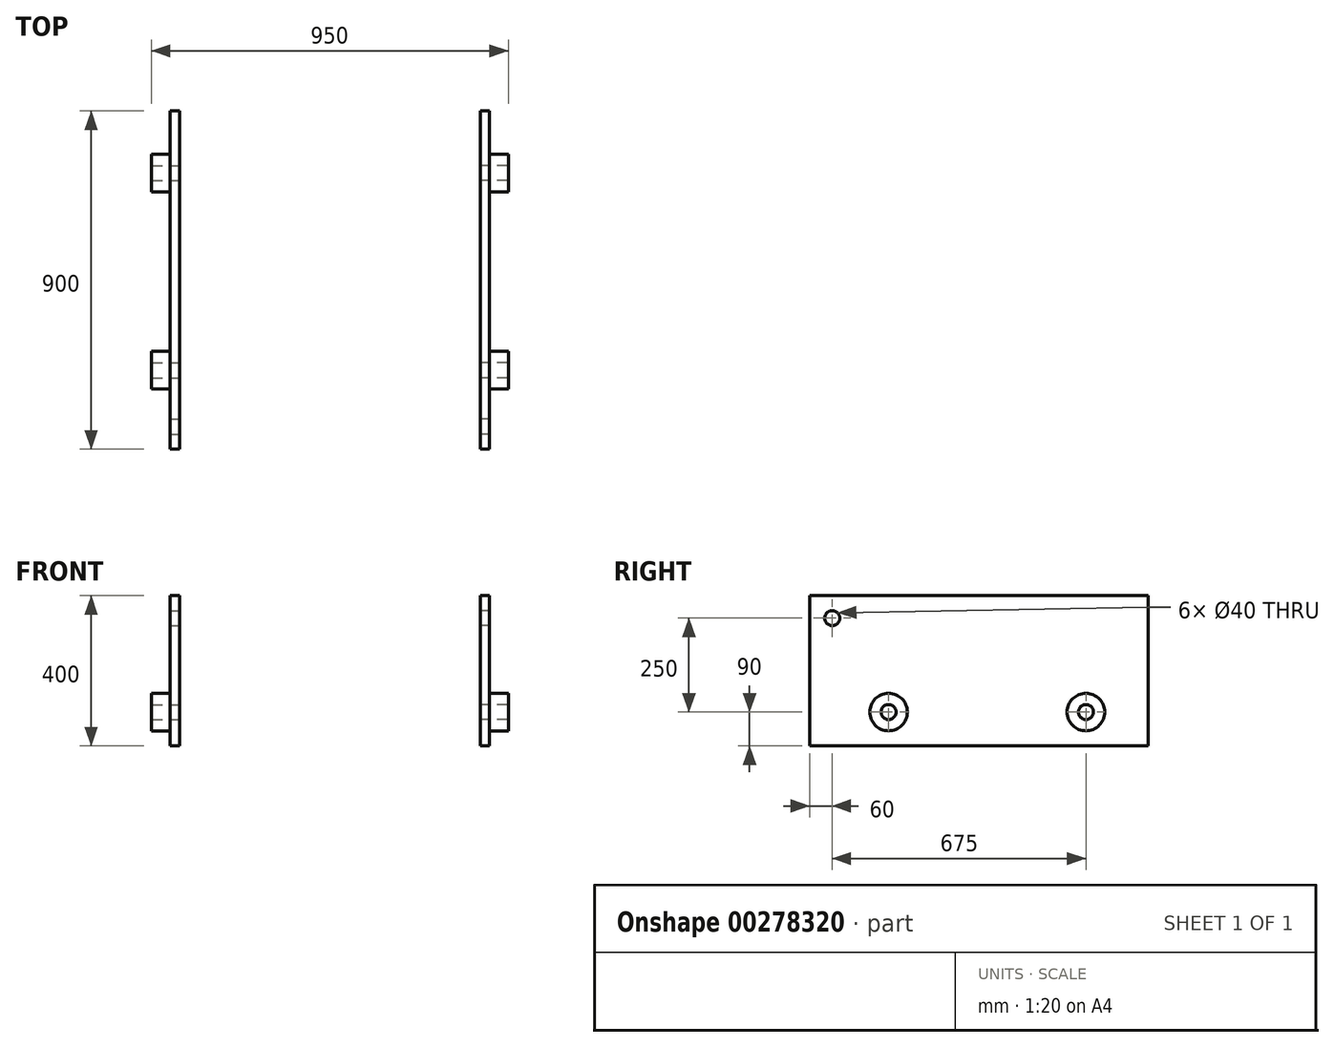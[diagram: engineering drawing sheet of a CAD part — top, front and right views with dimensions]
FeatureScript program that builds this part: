
annotation { "Feature Type Name" : "Feature", "Feature Type Description" : "" }
export const myFeature = defineFeature(function(context is Context, id is Id, definition is map)
    precondition{}
    {
        {
            var Q0;
            Q0=qCreatedBy(makeId("Right.planeOp"),FACE);
            var sketch = newSketch(context, id + "F0", { "sketchPlane" : qUnion([Q0])});
            skLineSegment(sketch, "E0.bottom", {"start": v(0, 0) * mm, "end": v(900, 0) * mm});
            skLineSegment(sketch, "E0.top", {"start": v(0, 400) * mm, "end": v(900, 400) * mm});
            skLineSegment(sketch, "E0.left", {"start": v(0, 0) * mm, "end": v(0, 400) * mm});
            skLineSegment(sketch, "E0.right", {"start": v(900, 0) * mm, "end": v(900, 400) * mm});
            skCircle(sketch, "E1", {"center": v(60, 340) * mm, "radius": 20 * mm});
            skCircle(sketch, "E2", {"center": v(210, 90) * mm, "radius": 20 * mm});
            skCircle(sketch, "E3", {"center": v(735, 90) * mm, "radius": 20 * mm});
            skSolve(sketch);
        }
        {
            var Q0;
            Q0=makeQuery(id+"F0.imprint","IMPRINT",FACE,{"disambiguationData":[TD([[makeQuery(id+"F0.imprint","IMPRINT",EDGE,{"derivedFrom":sQuery(id+"F0.wireOp",EDGE,"E0.bottom")}),1.0]])]});
            extrude(context, id + "F1", {"entities" : qUnion([Q0]), "depth" : 25 * mm});
        }
        {
            var Q0;
            Q0=makeQuery(id+"F1.opExtrude","CAP_FACE",FACE,{"disambiguationData":[OSD([sQuery(id+"F0.wireOp",EDGE,"E0.bottom"),sQuery(id+"F0.wireOp",EDGE,"E0.top"),sQuery(id+"F0.wireOp",EDGE,"E0.left"),sQuery(id+"F0.wireOp",EDGE,"E0.right"),sQuery(id+"F0.wireOp",EDGE,"E1"),sQuery(id+"F0.wireOp",EDGE,"E2"),sQuery(id+"F0.wireOp",EDGE,"E3")])],"isStart":false});
            var sketch = newSketch(context, id + "F2", { "sketchPlane" : qUnion([Q0])});
            skCircle(sketch, "E4", {"center": v(210, 90) * mm, "radius": 50 * mm});
            skCircle(sketch, "E5", {"center": v(735, 90) * mm, "radius": 50 * mm});
            skSolve(sketch);
        }
        {
            var Q0;
            Q0=makeQuery(id+"F2.imprint","IMPRINT",FACE,{"disambiguationData":[TD([[makeQuery(id+"F2.imprint","IMPRINT",EDGE,{"derivedFrom":sQuery(id+"F2.wireOp",EDGE,"E4")}),1.0]])]});
            var Q1;
            Q1=makeQuery(id+"F2.imprint","IMPRINT",FACE,{"disambiguationData":[TD([[makeQuery(id+"F2.imprint","IMPRINT",EDGE,{"derivedFrom":sQuery(id+"F2.wireOp",EDGE,"E5")}),1.0]])]});
            extrude(context, id + "F3", {"entities" : qUnion([Q0, Q1]), "operationType" : NewBodyOperationType.ADD, "depth" : 50 * mm});
        }
        {
            var Q0;
            Q0=makeQuery(id+"F1.opExtrude","CAP_FACE",FACE,{"disambiguationData":[OSD([sQuery(id+"F0.wireOp",EDGE,"E0.bottom"),sQuery(id+"F0.wireOp",EDGE,"E0.top"),sQuery(id+"F0.wireOp",EDGE,"E0.left"),sQuery(id+"F0.wireOp",EDGE,"E0.right"),sQuery(id+"F0.wireOp",EDGE,"E1"),sQuery(id+"F0.wireOp",EDGE,"E2"),sQuery(id+"F0.wireOp",EDGE,"E3")])],"isStart":true});
            cPlane(context, id + "F4", {"entities" : qUnion([Q0]), "cplaneType" : CPlaneType.OFFSET, "offset" : 400 * mm, "width" : 150 * mm, "height" : 150 * mm});
        }
        {
            var Q0;
            Q0=makeQuery(id+"F1.opExtrude","SWEPT_BODY",BODY,{"disambiguationData":[OSD([sQuery(id+"F0.wireOp",EDGE,"E0.bottom"),sQuery(id+"F0.wireOp",EDGE,"E0.top"),sQuery(id+"F0.wireOp",EDGE,"E0.left"),sQuery(id+"F0.wireOp",EDGE,"E0.right"),sQuery(id+"F0.wireOp",EDGE,"E1"),sQuery(id+"F0.wireOp",EDGE,"E2"),sQuery(id+"F0.wireOp",EDGE,"E3")])]});
            var Q1;
            Q1=qCreatedBy(id+"F4.planeOp",FACE);
            mirror(context, id + "F5", {"entities" : qUnion([Q0]), "mirrorPlane" : qUnion([Q1])});
        }
    });
